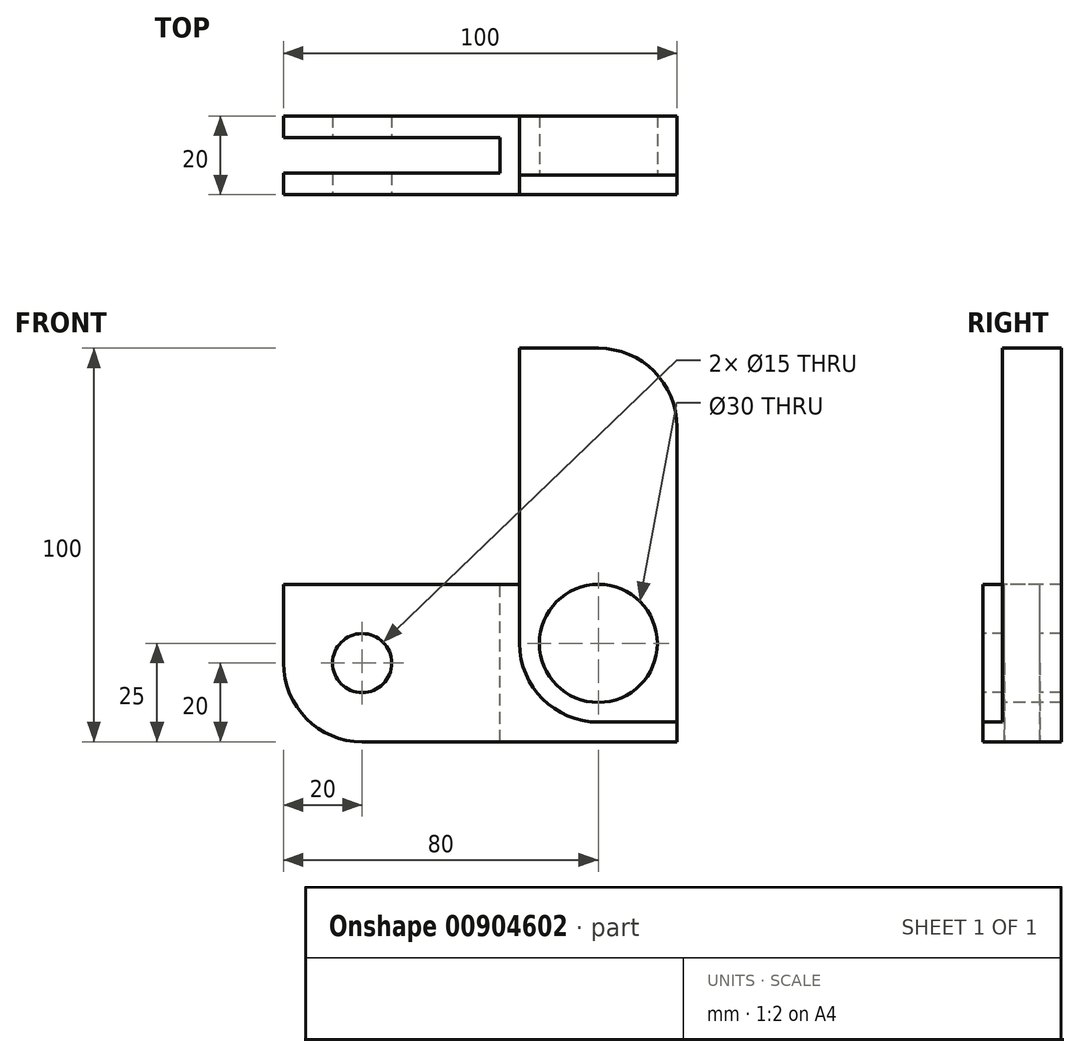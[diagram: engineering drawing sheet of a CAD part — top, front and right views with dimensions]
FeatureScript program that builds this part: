
annotation { "Feature Type Name" : "Feature", "Feature Type Description" : "" }
export const myFeature = defineFeature(function(context is Context, id is Id, definition is map)
    precondition{}
    {
        {
            var Q0;
            Q0=qCreatedBy(makeId("Front.planeOp"),FACE);
            var sketch = newSketch(context, id + "F0", { "sketchPlane" : qUnion([Q0])});
            skLineSegment(sketch, "E0.bottom", {"start": v(0, 0) * mm, "end": v(100, 0) * mm});
            skLineSegment(sketch, "E0.top", {"start": v(0, 100) * mm, "end": v(100, 100) * mm});
            skLineSegment(sketch, "E0.left", {"start": v(0, 0) * mm, "end": v(0, 100) * mm});
            skLineSegment(sketch, "E0.right", {"start": v(100, 0) * mm, "end": v(100, 100) * mm});
            skSolve(sketch);
        }
        {
            var Q0;
            Q0=makeQuery(id+"F0.imprint","IMPRINT",FACE,{"disambiguationData":[TD([[makeQuery(id+"F0.imprint","IMPRINT",EDGE,{"derivedFrom":sQuery(id+"F0.wireOp",EDGE,"E0.bottom")}),1.0]])]});
            extrude(context, id + "F1", {"entities" : qUnion([Q0]), "depth" : 20 * mm, "offsetDistance" : 25 * mm});
        }
        {
            var Q0;
            Q0=makeQuery(id+"F1.opExtrude","CAP_FACE",FACE,{"disambiguationData":[OSD([sQuery(id+"F0.wireOp",EDGE,"E0.bottom"),sQuery(id+"F0.wireOp",EDGE,"E0.top"),sQuery(id+"F0.wireOp",EDGE,"E0.left"),sQuery(id+"F0.wireOp",EDGE,"E0.right")])],"isStart":false});
            var sketch = newSketch(context, id + "F2", { "sketchPlane" : qUnion([Q0])});
            skCircle(sketch, "E1", {"center": v(20, 20) * mm, "radius": 7.5 * mm});
            skCircle(sketch, "E2", {"center": v(80, 25) * mm, "radius": 15 * mm});
            skSolve(sketch);
        }
        {
            var Q0;
            Q0=makeQuery(id+"F2.imprint","IMPRINT",FACE,{"disambiguationData":[TD([[makeQuery(id+"F2.imprint","IMPRINT",EDGE,{"derivedFrom":sQuery(id+"F2.wireOp",EDGE,"E1")}),1.0]])]});
            var Q1;
            Q1=makeQuery(id+"F2.imprint","IMPRINT",FACE,{"disambiguationData":[TD([[makeQuery(id+"F2.imprint","IMPRINT",EDGE,{"derivedFrom":sQuery(id+"F2.wireOp",EDGE,"E2")}),1.0]])]});
            extrude(context, id + "F3", {"entities" : qUnion([Q0, Q1]), "operationType" : NewBodyOperationType.REMOVE, "endBound" : BoundingType.THROUGH_ALL, "oppositeDirection" : true, "depth" : 25 * mm, "offsetDistance" : 25 * mm});
        }
        {
            var Q0;
            Q0=makeQuery(id+"F1.opExtrude","CAP_FACE",FACE,{"disambiguationData":[OSD([sQuery(id+"F0.wireOp",EDGE,"E0.bottom"),sQuery(id+"F0.wireOp",EDGE,"E0.top"),sQuery(id+"F0.wireOp",EDGE,"E0.left"),sQuery(id+"F0.wireOp",EDGE,"E0.right")])],"isStart":false});
            var sketch = newSketch(context, id + "F4", { "sketchPlane" : qUnion([Q0])});
            skLineSegment(sketch, "E3.bottom", {"start": v(0, 100) * mm, "end": v(60, 100) * mm});
            skLineSegment(sketch, "E3.top", {"start": v(0, 40) * mm, "end": v(60, 40) * mm});
            skLineSegment(sketch, "E3.left", {"start": v(0, 100) * mm, "end": v(0, 40) * mm});
            skLineSegment(sketch, "E3.right", {"start": v(60, 100) * mm, "end": v(60, 40) * mm});
            skSolve(sketch);
        }
        {
            var Q0;
            Q0=makeQuery(id+"F4.imprint","IMPRINT",FACE,{"disambiguationData":[TD([[makeQuery(id+"F4.imprint","IMPRINT",EDGE,{"derivedFrom":sQuery(id+"F4.wireOp",EDGE,"E3.bottom")}),-1.0]])]});
            extrude(context, id + "F5", {"entities" : qUnion([Q0]), "operationType" : NewBodyOperationType.REMOVE, "endBound" : BoundingType.THROUGH_ALL, "oppositeDirection" : true, "depth" : 25 * mm, "offsetDistance" : 25 * mm});
        }
        {
            var Q0;
            Q0=makeQuery(id+"F1.opExtrude","CAP_FACE",FACE,{"disambiguationData":[OSD([sQuery(id+"F0.wireOp",EDGE,"E0.bottom"),sQuery(id+"F0.wireOp",EDGE,"E0.top"),sQuery(id+"F0.wireOp",EDGE,"E0.left"),sQuery(id+"F0.wireOp",EDGE,"E0.right")])],"isStart":false});
            var sketch = newSketch(context, id + "F6", { "sketchPlane" : qUnion([Q0])});
            skLineSegment(sketch, "E4.bottom", {"start": v(60, 100) * mm, "end": v(100, 100) * mm});
            skLineSegment(sketch, "E4.top", {"start": v(60, 5) * mm, "end": v(100, 5) * mm});
            skLineSegment(sketch, "E4.left", {"start": v(60, 100) * mm, "end": v(60, 5) * mm});
            skLineSegment(sketch, "E4.right", {"start": v(100, 100) * mm, "end": v(100, 5) * mm});
            skSolve(sketch);
        }
        {
            var Q0;
            {var subQ3=sQuery(id+"F6.wireOp",EDGE,"E4.bottom");Q0=makeQuery(id+"F6.imprint","IMPRINT",FACE,{"disambiguationData":[TD([[makeQuery(id+"F6.imprint","IMPRINT",EDGE,{"derivedFrom":subQ3}),-1.0]])]});}
            extrude(context, id + "F7", {"entities" : qUnion([Q0]), "operationType" : NewBodyOperationType.REMOVE, "oppositeDirection" : true, "depth" : 5 * mm, "offsetDistance" : 25 * mm});
        }
        {
            var Q0;
            Q0=qCreatedBy(makeId("Front.planeOp"),FACE);
            cPlane(context, id + "F8", {"entities" : qUnion([Q0]), "cplaneType" : CPlaneType.OFFSET, "offset" : 10 * mm, "width" : 150 * mm, "height" : 150 * mm});
        }
        {
            var Q0;
            Q0=makeQuery(id+"F1.opExtrude","SWEPT_EDGE",EDGE,{"disambiguationData":[OSD([sQuery(id+"F0.wireOp",EDGE,"E0.top"),sQuery(id+"F0.wireOp",EDGE,"E0.right")])]});
            var Q1;
            Q1=makeQuery(id+"F5.boolean.opBoolean","COPY",EDGE,{"derivedFrom":makeQuery(id+"F5.opExtrude","SWEPT_EDGE",EDGE,{"disambiguationData":[OSD([sQuery(id+"F0.wireOp",EDGE,"E0.top"),sQuery(id+"F4.wireOp",EDGE,"E3.bottom"),sQuery(id+"F4.wireOp",EDGE,"E3.right")])]})});
            fillet(context, id + "F9", {"entities" : qUnion([Q0, Q1]), "radius" : 20 * mm, "tangentPropagation" : true, "allowEdgeOverflow" : false});
        }
        {
            var Q0;
            Q0=makeQuery(id+"F5.boolean.opBoolean","COPY",EDGE,{"derivedFrom":makeQuery(id+"F5.opExtrude","SWEPT_EDGE",EDGE,{"disambiguationData":[OSD([sQuery(id+"F0.wireOp",EDGE,"E0.left"),sQuery(id+"F4.wireOp",EDGE,"E3.top"),sQuery(id+"F4.wireOp",EDGE,"E3.left")])]})});
            var Q1;
            Q1=makeQuery(id+"F1.opExtrude","SWEPT_EDGE",EDGE,{"disambiguationData":[OSD([sQuery(id+"F0.wireOp",EDGE,"E0.bottom"),sQuery(id+"F0.wireOp",EDGE,"E0.left")])]});
            fillet(context, id + "F10", {"entities" : qUnion([Q0, Q1]), "radius" : 20 * mm, "tangentPropagation" : true, "allowEdgeOverflow" : false});
        }
        {
            var Q0;
            Q0=makeQuery(id+"F7.boolean.opBoolean","COPY",EDGE,{"derivedFrom":makeQuery(id+"F7.opExtrude","SWEPT_EDGE",EDGE,{"disambiguationData":[OSD([sQuery(id+"F6.wireOp",EDGE,"E4.top"),sQuery(id+"F6.wireOp",EDGE,"E4.left")])]})});
            var Q1;
            Q1=makeQuery(id+"FIZr4OldzpWijIq_1.1.F7.boolean.opBoolean","COPY",EDGE,{"derivedFrom":makeQuery(id+"FIZr4OldzpWijIq_1.1.F7.opExtrude","SWEPT_EDGE",EDGE,{"disambiguationData":[OSD([sQuery(id+"F6.wireOp",EDGE,"E4.top"),sQuery(id+"F6.wireOp",EDGE,"E4.left")])]})});
            fillet(context, id + "F11", {"entities" : qUnion([Q0, Q1]), "radius" : 20 * mm, "tangentPropagation" : true, "allowEdgeOverflow" : false});
        }
        {
            var Q0;
            Q0=makeQuery(id+"F5.boolean.opBoolean","COPY",FACE,{"derivedFrom":makeQuery(id+"F5.opExtrude","SWEPT_FACE",FACE,{"disambiguationData":[OSD([sQuery(id+"F4.wireOp",EDGE,"E3.top")])]})});
            var sketch = newSketch(context, id + "F12", { "sketchPlane" : qUnion([Q0])});
            skLineSegment(sketch, "E5.bottom", {"start": v(0, -5.45) * mm, "end": v(55, -5.45) * mm});
            skLineSegment(sketch, "E5.top", {"start": v(0, -14.55) * mm, "end": v(55, -14.55) * mm});
            skLineSegment(sketch, "E5.left", {"start": v(0, -5.45) * mm, "end": v(0, -14.55) * mm});
            skLineSegment(sketch, "E5.right", {"start": v(55, -5.45) * mm, "end": v(55, -14.55) * mm});
            skSolve(sketch);
        }
        {
            var Q0;
            {var subQ0=sQuery(id+"F12.wireOp",EDGE,"E5.right");Q0=makeQuery(id+"F12.imprint","IMPRINT",FACE,{"disambiguationData":[TD([[makeQuery(id+"F12.imprint","IMPRINT",EDGE,{"derivedFrom":subQ0}),-1.0]])]});}
            var Q1;
            {var subQ0=sQuery(id+"F12.wireOp",EDGE,"E5.left");Q1=makeQuery(id+"F12.imprint","IMPRINT",FACE,{"disambiguationData":[TD([[makeQuery(id+"F12.imprint","IMPRINT",EDGE,{"derivedFrom":subQ0}),1.0]])]});}
            extrude(context, id + "F13", {"entities" : qUnion([Q0, Q1]), "operationType" : NewBodyOperationType.REMOVE, "endBound" : BoundingType.THROUGH_ALL, "oppositeDirection" : true, "depth" : 25 * mm, "offsetDistance" : 25 * mm});
        }
    });
